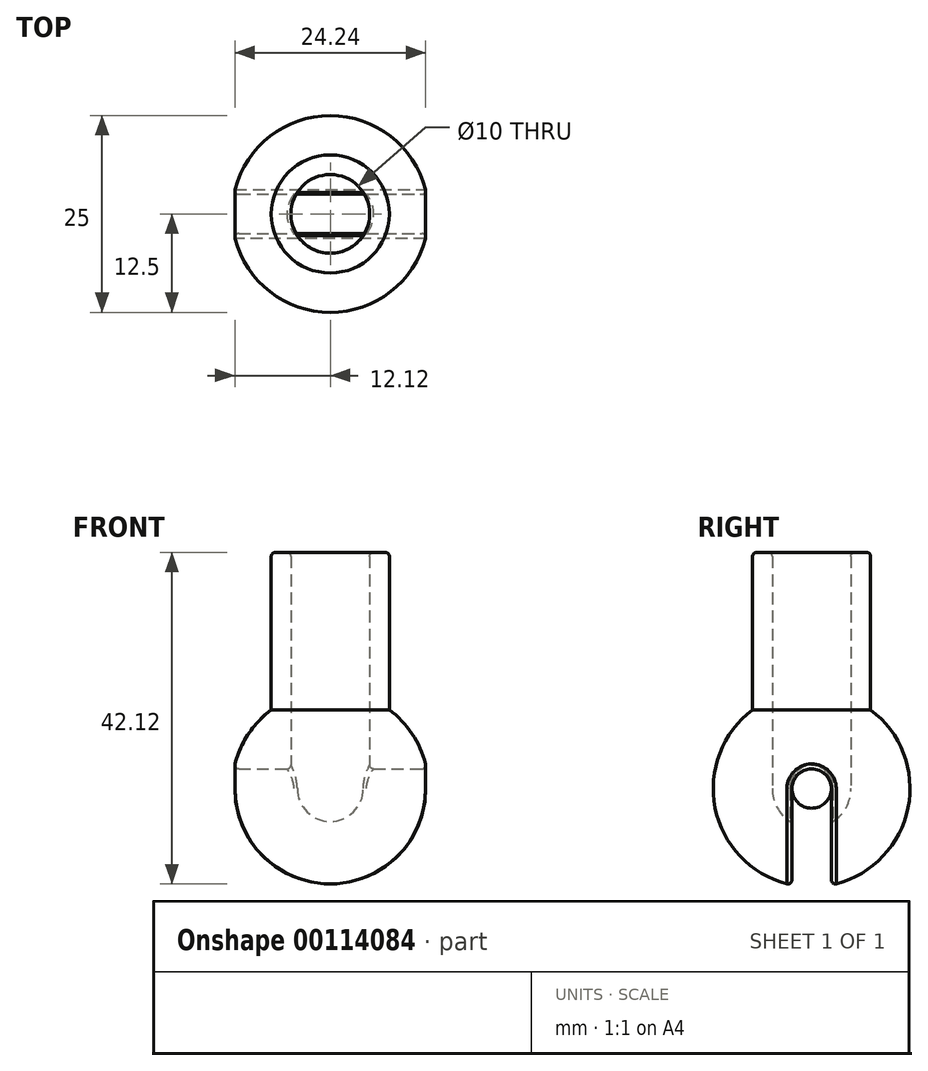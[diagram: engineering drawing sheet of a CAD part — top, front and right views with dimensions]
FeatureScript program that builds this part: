
annotation { "Feature Type Name" : "Feature", "Feature Type Description" : "" }
export const myFeature = defineFeature(function(context is Context, id is Id, definition is map)
    precondition{}
    {
        {
            var Q0;
            Q0=qCreatedBy(makeId("Front.planeOp"),FACE);
            var sketch = newSketch(context, id + "F0", { "sketchPlane" : qUnion([Q0])});
            skArc(sketch, "E0", {"start": v(0, 0) * mm, "mid": v(11.86, 8.55) * mm, "end": v(7.5, 22.5) * mm});
            skArc(sketch, "E1", {"start": v(0, 7.5) * mm, "mid": v(3.54, 8.96) * mm, "end": v(5, 12.5) * mm});
            skLineSegment(sketch, "E2", {"start": v(7.5, 42.5) * mm, "end": v(7.5, 22.5) * mm});
            skLineSegment(sketch, "E3", {"start": v(0, 0) * mm, "end": v(0, 50.88) * mm, "construction": true});
            skLineSegment(sketch, "E4.trimOffspring", {"start": v(5, 42.5) * mm, "end": v(7.5, 42.5) * mm});
            skLineSegment(sketch, "E5", {"start": v(5, 12.5) * mm, "end": v(5, 42.5) * mm});
            skLineSegment(sketch, "E6", {"start": v(0, 7.5) * mm, "end": v(0, 0) * mm});
            skSolve(sketch);
        }
        {
            var Q0;
            Q0 = qSketchRegion(id + "F0", true);
            var Q1;
            Q1=sQuery(id+"F0.wireOp",EDGE,"E3");
            revolve(context, id + "F1", {"entities" : qUnion([Q0]), "axis" : qUnion([Q1]), "revolveType" : RevolveType.FULL});
        }
        {
            var Q0;
            Q0=qCreatedBy(makeId("Right.planeOp"),FACE);
            var sketch = newSketch(context, id + "F2", { "sketchPlane" : qUnion([Q0])});
            skCircle(sketch, "E7", {"center": v(0, 12.5) * mm, "radius": 12.5 * mm, "construction": true});
            skArc(sketch, "E8", {"start": v(2.5, 12.5) * mm, "mid": v(0, 15) * mm, "end": v(-2.5, 12.5) * mm});
            skLineSegment(sketch, "E9", {"start": v(-2.5, 12.5) * mm, "end": v(-2.5, 0) * mm});
            skLineSegment(sketch, "E10", {"start": v(2.5, 12.5) * mm, "end": v(2.5, 0) * mm});
            skLineSegment(sketch, "E11", {"start": v(2.5, 0) * mm, "end": v(-2.5, 0) * mm});
            skSolve(sketch);
        }
        {
            var Q0;
            Q0 = qSketchRegion(id + "F2", true);
            var Q1;
            Q1=makeQuery(id+"F1.opRevolve","SWEPT_FACE",FACE,{"disambiguationData":[OSD([sQuery(id+"F0.wireOp",EDGE,"E0")])]});
            extrude(context, id + "F3", {"entities" : qUnion([Q0]), "operationType" : NewBodyOperationType.REMOVE, "endBound" : BoundingType.THROUGH_ALL, "oppositeDirection" : true, "depth" : 25 * mm, "hasSecondDirection" : true, "secondDirectionBound" : SecondDirectionBoundingType.THROUGH_ALL, "secondDirectionOppositeDirection" : false, "secondDirectionBoundEntityFace" : qUnion([Q1]), "secondDirectionDepth" : 25 * mm});
        }
        {
            var Q0;
            Q0=makeQuery(id+"F1.opRevolve","SWEPT_EDGE",EDGE,{"disambiguationData":[OSD([sQuery(id+"F0.wireOp",EDGE,"E2"),sQuery(id+"F0.wireOp",EDGE,"E4.trimOffspring")])]});
            var Q1;
            Q1=makeQuery(id+"F1.opRevolve","SWEPT_EDGE",EDGE,{"disambiguationData":[OSD([sQuery(id+"F0.wireOp",EDGE,"E4.trimOffspring"),sQuery(id+"F0.wireOp",EDGE,"E5")])]});
            var Q2;
            Q2=makeQuery(id+"F3.boolean.opBoolean","INTERSECT",EDGE,{"derivedFrom":[makeQuery(id+"F1.opRevolve","SWEPT_FACE",FACE,{"disambiguationData":[OSD([sQuery(id+"F0.wireOp",EDGE,"E1")])]}),makeQuery(id+"F3.opExtrude","SWEPT_FACE",FACE,{"disambiguationData":[OSD([sQuery(id+"F2.wireOp",EDGE,"E9")])]})]});
            var Q3;
            Q3=makeQuery(id+"F3.boolean.opBoolean","INTERSECT",EDGE,{"derivedFrom":[makeQuery(id+"F1.opRevolve","SWEPT_FACE",FACE,{"disambiguationData":[OSD([sQuery(id+"F0.wireOp",EDGE,"E0")])]}),makeQuery(id+"F3.opExtrude","SWEPT_FACE",FACE,{"disambiguationData":[OSD([sQuery(id+"F2.wireOp",EDGE,"E10")])]})]});
            fillet(context, id + "F4", {"entities" : qUnion([Q0, Q1, Q2, Q3]), "radius" : 0.5 * mm, "tangentPropagation" : true, "allowEdgeOverflow" : false});
        }
    });
